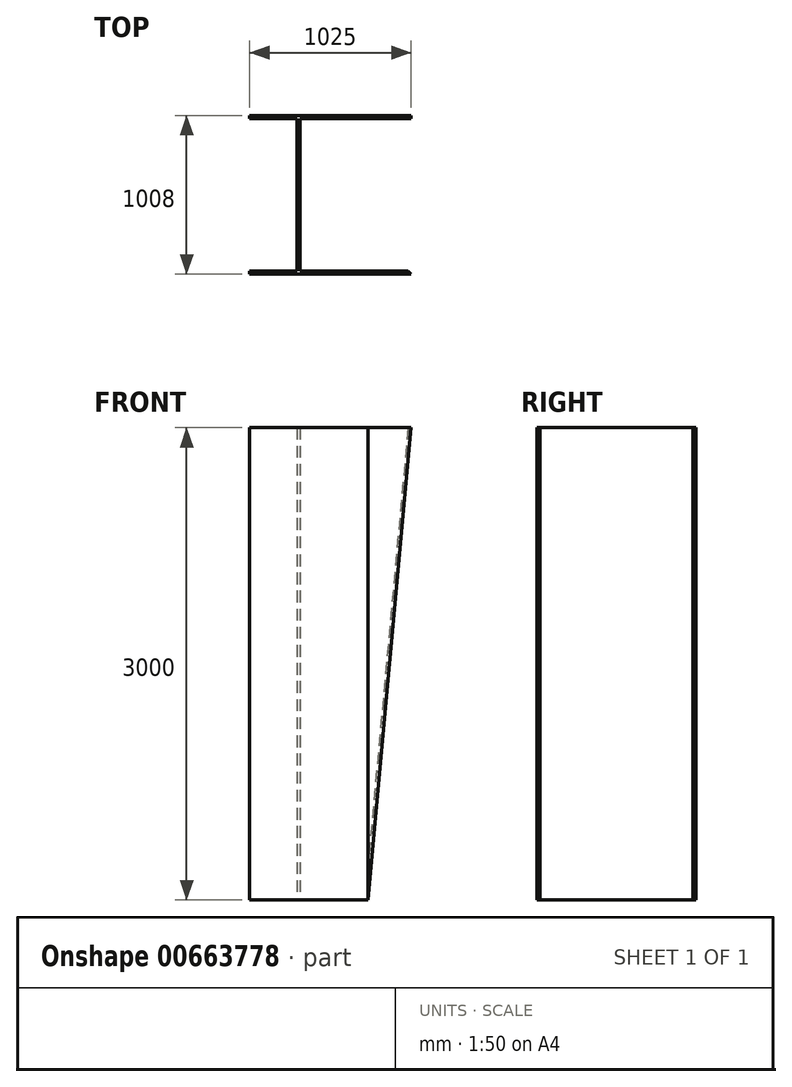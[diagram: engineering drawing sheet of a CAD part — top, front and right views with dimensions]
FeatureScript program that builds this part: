
annotation { "Feature Type Name" : "Feature", "Feature Type Description" : "" }
export const myFeature = defineFeature(function(context is Context, id is Id, definition is map)
    precondition{}
    {
        {
            var Q0;
            Q0=qCreatedBy(makeId("Top.planeOp"),FACE);
            var sketch = newSketch(context, id + "F0", { "sketchPlane" : qUnion([Q0])});
            skLineSegment(sketch, "E0", {"start": v(0, 0) * mm, "end": v(750, 0) * mm});
            skLineSegment(sketch, "E1", {"start": v(750, 0) * mm, "end": v(750, 19) * mm});
            skLineSegment(sketch, "E2", {"start": v(0, 0) * mm, "end": v(0, 19) * mm});
            skLineSegment(sketch, "E3", {"start": v(300, 19) * mm, "end": v(300, 989) * mm});
            skLineSegment(sketch, "E4", {"start": v(319, 989) * mm, "end": v(319, 19) * mm});
            skLineSegment(sketch, "E5.trimOffspring", {"start": v(319, 19) * mm, "end": v(750, 19) * mm});
            skLineSegment(sketch, "E6", {"start": v(0, 19) * mm, "end": v(300, 19) * mm});
            skLineSegment(sketch, "E7", {"start": v(300, 989) * mm, "end": v(0, 989) * mm});
            skLineSegment(sketch, "E8", {"start": v(0, 989) * mm, "end": v(0, 1008) * mm});
            skLineSegment(sketch, "E9", {"start": v(0, 1008) * mm, "end": v(750, 1008) * mm});
            skLineSegment(sketch, "E10", {"start": v(750, 1008) * mm, "end": v(750, 989) * mm});
            skLineSegment(sketch, "E11", {"start": v(750, 989) * mm, "end": v(319, 989) * mm});
            skSolve(sketch);
        }
        {
            var Q0;
            Q0 = qSketchRegion(id + "F0", true);
            extrude(context, id + "F1", {"entities" : qUnion([Q0]), "depth" : 3000 * mm, "offsetDistance" : 25 * mm});
        }
        {
            var Q0;
            Q0=makeQuery(id+"F1.opExtrude","SWEPT_FACE",FACE,{"disambiguationData":[OSD([sQuery(id+"F0.wireOp",EDGE,"E0")])]});
            var sketch = newSketch(context, id + "F2", { "sketchPlane" : qUnion([Q0])});
            skLineSegment(sketch, "E12", {"start": v(750, 3000) * mm, "end": v(1025, 3000) * mm});
            skLineSegment(sketch, "E13", {"start": v(1025, 3000) * mm, "end": v(750, 0) * mm});
            skLineSegment(sketch, "E14", {"start": v(750, 0) * mm, "end": v(750, 3000) * mm});
            skSolve(sketch);
        }
        {
            var Q0;
            Q0 = qSketchRegion(id + "F2", true);
            extrude(context, id + "F3", {"entities" : qUnion([Q0]), "oppositeDirection" : true, "depth" : 19 * mm, "offsetDistance" : 25 * mm});
        }
        {
            var Q0;
            Q0=makeQuery(id+"F1.opExtrude","SWEPT_FACE",FACE,{"disambiguationData":[OSD([sQuery(id+"F0.wireOp",EDGE,"E9")])]});
            var sketch = newSketch(context, id + "F4", { "sketchPlane" : qUnion([Q0])});
            skLineSegment(sketch, "E15", {"start": v(-750, 3000) * mm, "end": v(-1025, 3000) * mm});
            skLineSegment(sketch, "E16", {"start": v(-1025, 3000) * mm, "end": v(-750, 0) * mm});
            skLineSegment(sketch, "E17", {"start": v(-750, 0) * mm, "end": v(-750, 3000) * mm});
            skSolve(sketch);
        }
        {
            var Q0;
            Q0 = qSketchRegion(id + "F4", true);
            extrude(context, id + "F5", {"entities" : qUnion([Q0]), "oppositeDirection" : true, "depth" : 19 * mm, "offsetDistance" : 25 * mm});
        }
        {
            var Q0;
            Q0=makeQuery(id+"F3.opExtrude","CAP_EDGE",EDGE,{"disambiguationData":[OSD([sQuery(id+"F2.wireOp",EDGE,"E13")])],"isStart":false});
            chamfer(context, id + "F6", {"entities" : qUnion([Q0]), "width" : 19 * mm, "tangentPropagation" : true});
        }
    });
